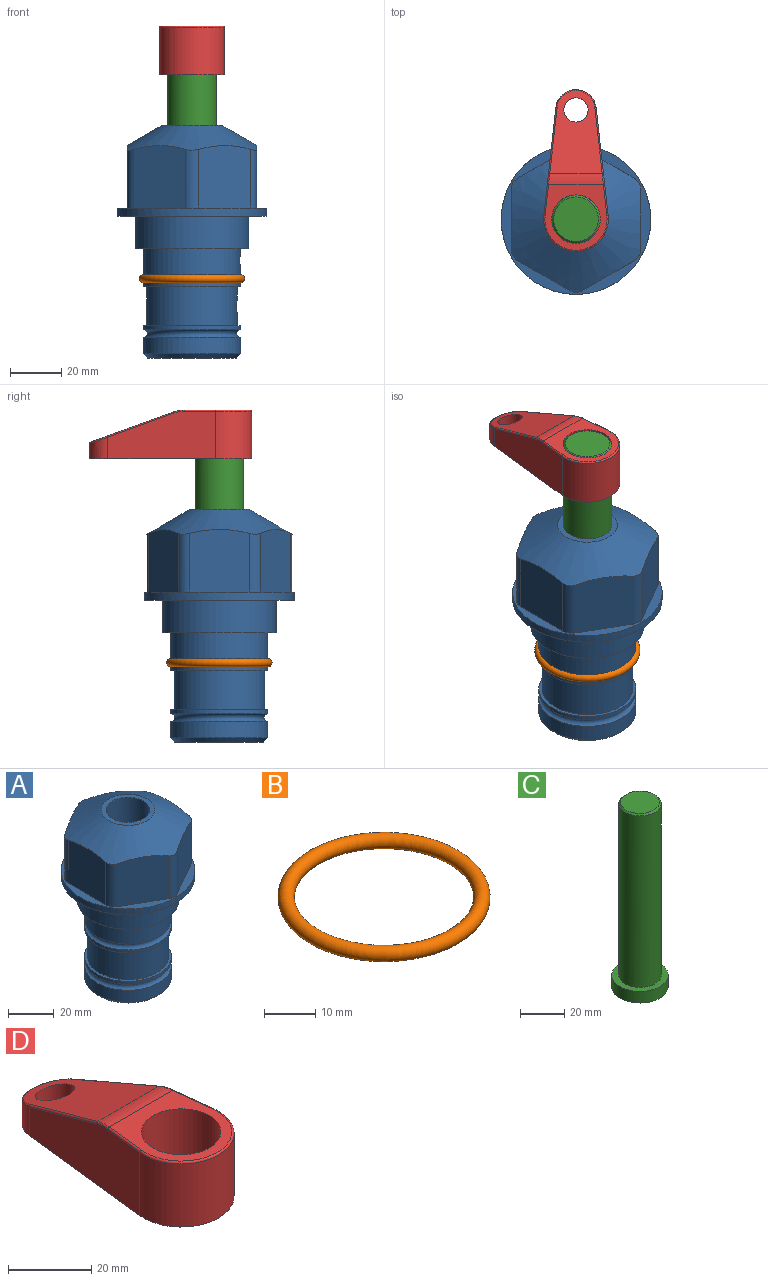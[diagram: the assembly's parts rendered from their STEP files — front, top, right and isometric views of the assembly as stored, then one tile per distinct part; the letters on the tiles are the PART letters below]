
ASSEMBLY  parts=4 mates=2
PART A: 36 faces, bbox 58.7x58.7x91.2 mm
  f0: cylinder r=17.78mm len=35.56mm, axis (0,0,1), area 1670.8mm2, adj f23,f24,f31
  f1: cylinder r=19.05mm len=38.1mm, axis (0,0,1), area 1191.9mm2, adj f26,f27,f30
  f2: plane 58.66x58.66mm, normal (0,0,-1), area 1150.6mm2, adj f3,f28
  f3: cylinder r=29.33mm len=58.66mm, axis (0,0,-1), area 585.1mm2, adj f2,f4
  f4: plane 58.66x58.66mm, normal (0,0,1), area 475.9mm2, adj f3,f5,f6,f7,f8,f9,f10,f11
  f5: plane 24.5x20.32mm, normal (-0.5,0.87,0), area 562.8mm2, adj f4,f15,f16,f17
  f6: plane 24.5x20.32mm, normal (0.5,0.87,0), area 562.8mm2, adj f4,f14,f15,f17
  f7: plane 24.5x23.48mm, normal (1,0,0), area 562.8mm2, adj f4,f13,f14,f17
  f8: plane 24.5x20.32mm, normal (0.5,-0.87,0), area 562.8mm2, adj f4,f12,f13,f17
  f9: plane 24.5x20.32mm, normal (-0.5,-0.87,0), area 562.8mm2, adj f4,f11,f12,f17
  f10: plane 24.5x23.48mm, normal (-1,0,0), area 562.8mm2, adj f4,f11,f16,f17
  f11: cylinder r=5.08mm len=23.01mm, axis (0,0,-1), area 121.2mm2, adj f4,f9,f10,f17
  f12: cylinder r=5.08mm len=23.01mm, axis (0,0,-1), area 121.2mm2, adj f4,f8,f9,f17
  f13: cylinder r=5.08mm len=23.01mm, axis (0,0,-1), area 121.2mm2, adj f4,f7,f8,f17
  f14: cylinder r=5.08mm len=23.01mm, axis (0,0,-1), area 121.2mm2, adj f4,f6,f7,f17
  f15: cylinder r=5.08mm len=23.01mm, axis (0,0,-1), area 121.2mm2, adj f4,f5,f6,f17
  f16: cylinder r=5.08mm len=23.01mm, axis (0,0,-1), area 121.2mm2, adj f4,f5,f10,f17
  f17: cone r=11.73mm half-angle=60deg, axis (0,0,-1), area 2071.8mm2, adj f5,f6,f7,f8,f9,f10,f11,f12
  f18: plane 23.46x23.46mm, normal (0,0,1), area 147.4mm2, adj f17,f35
  f19: plane 34.93x34.93mm, normal (0,0,-1), area 958mm2, adj f29
  f20: cylinder r=19.05mm len=38.1mm, axis (0,0,1), area 760.1mm2, adj f21,f29
  f21: torus R=19.05mm, axis (0,0,1), area 565.3mm2, adj f20,f22
  f22: cylinder r=19.05mm len=38.1mm, axis (0,0,1), area 190mm2, adj f21,f23
  f23: plane 38.1x38.1mm, normal (0,0,1), area 146.9mm2, adj f0,f22
  f24: plane 38.1x38.1mm, normal (0,0,-1), area 146.9mm2, adj f0,f25
  f25: cylinder r=19.05mm len=38.1mm, axis (0,0,1), area 190mm2, adj f24,f26
  f26: torus R=19.05mm, axis (0,0,1), area 565.3mm2, adj f1,f25
  f27: plane 44.45x44.45mm, normal (0,0,-1), area 411.7mm2, adj f1,f28
  f28: cylinder r=22.23mm len=44.45mm, axis (0,0,1), area 1773.5mm2, adj f2,f27
  f29: cone r=19.05mm half-angle=45deg, axis (0,0,1), area 257.5mm2, adj f19,f20
  f30: cylinder r=3.17mm len=6.75mm, axis (-1,0,0), area 128mm2, adj f1,f33
  f31: cylinder r=3.17mm len=6.35mm, axis (-1,0,0), area 102.5mm2, adj f0,f33
  f32: plane 25.4x25.4mm, normal (0,0,1), area 506.7mm2, adj f33
  f33: cylinder r=12.7mm len=66.42mm, axis (0,0,-1), area 5236.2mm2, adj f30,f31,f32,f34
  f34: cone r=9.53mm half-angle=30deg, axis (0,0,-1), area 443.4mm2, adj f33,f35
  f35: cylinder r=9.53mm len=19.05mm, axis (0,0,-1), area 849mm2, adj f18,f34
PART B: 1 faces, bbox 44.7x44.7x3.2 mm
  f0: torus R=19.05mm, axis (0,0,1), area 1193.9mm2
PART C: 6 faces, bbox 25.4x25.4x101.6 mm
  f0: plane 17.46x17.46mm, normal (0,0,1), area 239.5mm2, adj f5
  f1: plane 25.4x25.4mm, normal (0,0,-1), area 506.7mm2, adj f2
  f2: cylinder r=12.7mm len=25.4mm, axis (0,0,1), area 506.7mm2, adj f1,f3
  f3: plane 25.4x25.4mm, normal (0,0,1), area 221.7mm2, adj f2,f4
  f4: cylinder r=9.53mm len=94.46mm, axis (0,0,1), area 5653mm2, adj f3,f5
  f5: cone r=8.73mm half-angle=45deg, axis (0,0,-1), area 64.4mm2, adj f0,f4
PART D: 44 faces, bbox 27.5x64.5x19.1 mm
  f0: plane 2.3x0.95mm, normal (0,0,-1), area 1mm2, adj f25,f30,f34
  f1: plane 63.5x25.4mm, normal (0,0,-1), area 561.7mm2, adj f2,f3,f4,f5,f6,f7,f19,f20
  f2: cylinder r=12.7mm len=25.4mm, axis (0,0,-1), area 792.2mm2, adj f1,f3,f5,f13
  f3: plane 42.33x18.54mm, normal (0.99,0.11,0), area 647mm2, adj f1,f2,f4,f11,f12,f14
  f4: cylinder r=7.94mm len=15.78mm, axis (0,0,-1), area 158.6mm2, adj f1,f3,f5,f16
  f5: plane 42.33x18.54mm, normal (-0.99,0.11,0), area 647mm2, adj f1,f2,f4,f15,f17,f18
  f6: cylinder r=9.53mm len=19.05mm, axis (0,0,-1), area 1140.1mm2, adj f1,f8
  f7: cylinder r=4.76mm len=10.98mm, axis (0,0,-1), area 276.1mm2, adj f1,f9
  f8: plane 25.83x24.38mm, normal (0,0,1), area 262.2mm2, adj f6,f10,f11,f13,f15
  f9: plane 32.49x20.55mm, normal (0,0.34,0.94), area 489.9mm2, adj f7,f10,f14,f16,f18
  f10: cylinder r=12.7mm len=21.49mm, axis (-1,0,0), area 93.2mm2, adj f8,f9,f12,f17
  f11: cylinder r=0.51mm len=12.34mm, axis (0.11,-0.99,0), area 9.9mm2, adj f3,f8,f12,f13
  f12: bspline ~7.62x1.64mm, area 3.5mm2, adj f3,f10,f11,f14
  f13: torus R=12.19mm, axis (0,0,1), area 33.6mm2, adj f2,f8,f11,f15
  f14: cylinder r=0.51mm len=26.01mm, axis (0.1,-0.93,0.34), area 21.6mm2, adj f3,f9,f12,f16
  f15: cylinder r=0.51mm len=12.34mm, axis (0.11,0.99,0), area 9.9mm2, adj f5,f8,f13,f17
  f16: bspline ~15.78x7.05mm, area 15.7mm2, adj f4,f9,f14,f18
  f17: bspline ~7.62x1.64mm, area 3.5mm2, adj f5,f10,f15,f18
  f18: cylinder r=0.51mm len=26.01mm, axis (0.1,0.93,-0.34), area 21.6mm2, adj f5,f9,f16,f17
  f19: plane 21.6x14.29mm, normal (-0.99,-0.11,0), area 242.6mm2, adj f1,f26,f28,f34,f36,f38
  f20: plane 21.6x14.29mm, normal (0.99,-0.11,0), area 242.6mm2, adj f1,f27,f29,f37,f39,f41
  f21: cylinder r=12.7mm len=14.29mm, axis (0,0,-1), area 173.2mm2, adj f1,f26,f27,f30,f31,f33
  f22: cylinder r=7.94mm len=7.63mm, axis (0,0,-1), area 53.8mm2, adj f1,f28,f29,f42
  f23: plane 2.3x0.95mm, normal (0,0,-1), area 1mm2, adj f25,f33,f37
  f24: plane 17.94x12.32mm, normal (0,-0.34,-0.94), area 191.2mm2, adj f25,f38,f41,f42
  f25: cylinder r=9.53mm len=12.93mm, axis (-1,0,0), area 37.5mm2, adj f0,f23,f24,f31,f36,f39
  f26: cylinder r=1.59mm len=14.29mm, axis (0,0,-1), area 49mm2, adj f1,f19,f21,f32
  f27: cylinder r=1.59mm len=14.29mm, axis (0,0,-1), area 49mm2, adj f1,f20,f21,f35
  f28: cylinder r=1.59mm len=7.28mm, axis (0,0,-1), area 22.1mm2, adj f1,f19,f22,f40
  f29: cylinder r=1.59mm len=7.28mm, axis (0,0,-1), area 22.1mm2, adj f1,f20,f22,f43
  f30: torus R=14.29mm, axis (0,0,1), area 5.8mm2, adj f0,f21,f31,f32
  f31: bspline ~11.06x2.73mm, area 20.8mm2, adj f21,f25,f30,f33
  f32: sphere r=1.59mm, area 5.4mm2, adj f26,f30,f34
  f33: torus R=14.29mm, axis (0,0,1), area 5.8mm2, adj f21,f23,f31,f35
  f34: cylinder r=1.59mm len=1.68mm, axis (-0.11,0.99,0), area 2.4mm2, adj f0,f19,f32,f36
  f35: sphere r=1.59mm, area 5.4mm2, adj f27,f33,f37
  f36: bspline ~5.82x2.33mm, area 7.7mm2, adj f19,f25,f34,f38
  f37: cylinder r=1.59mm len=1.68mm, axis (0.11,0.99,0), area 2.4mm2, adj f20,f23,f35,f39
  f38: cylinder r=1.59mm len=18.33mm, axis (0.1,-0.93,0.34), area 46.7mm2, adj f19,f24,f36,f40
  f39: bspline ~5.82x2.33mm, area 7.7mm2, adj f20,f25,f37,f41
  f40: sphere r=1.59mm, area 3.6mm2, adj f28,f38,f42
  f41: cylinder r=1.59mm len=18.33mm, axis (0.1,0.93,-0.34), area 46.7mm2, adj f20,f24,f39,f43
  f42: bspline ~8.31x1.84mm, area 15.3mm2, adj f22,f24,f40,f43
  f43: sphere r=1.59mm, area 3.6mm2, adj f29,f41,f42
PLACE A at identity fixed
PLACE B at identity
PLACE C t=(0,0,0.87)mm
PLACE D t=(0,0,55.48)mm
MATE fastened D.f2 <-> C.f2  axis (0,0,-1) through (0,0,74.53)mm
MATE cylindrical C.f2 <-> A.f0  axis (0,0,1) through (0,0,26.51)mm
